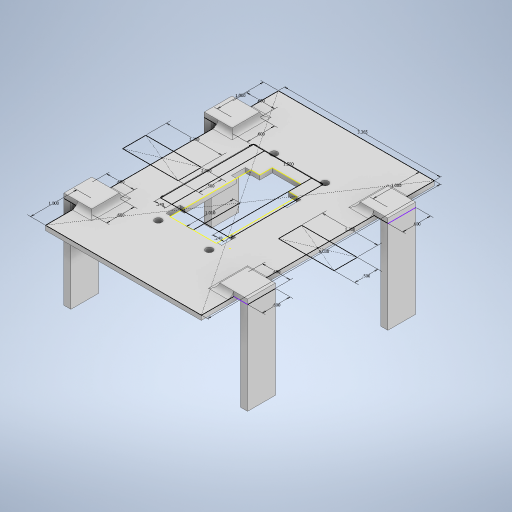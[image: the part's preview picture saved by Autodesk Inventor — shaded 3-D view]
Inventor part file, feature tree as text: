
AUTODESK INVENTOR PART (.ipt)
format: ipt  version: 2024.1 (Build 281209000, 209)  size: 502,272 bytes
history: native  units: in
note: dims shown in document units (in); Inventor stores cm internally (conversion verified against a paired STEP export)
features: extrude x10, sketch x9, projected_geometry x3, hole x2, fillet x2
ambient origin geometry x8: Origin, YZ Plane, XZ Plane, XY Plane, X Axis, Y Axis, Z Axis, Center Point
bodies: Solid1 (feature_tree)
feature tree (26):
  extrude  "Extrusion1"  Depth=2.0in
  extrude  "Extrusion2"  Depth=0.24in
  hole  "Hole1"  [1 undecoded]
  extrude  "Extrusion3"  Depth=1.0in TaperAngle=0.0deg
  extrude  "Extrusion4"  Depth=0.62in
  extrude  "Extrusion5"  Depth=2.02in
  sketch  "Sketch8"  dims[d18=0.5in d19=0.0in d20=0.62in]
  extrude  "Extrusion6"  Depth=1.75in
  sketch  "Sketch6"  dims[d8=0.5in]
  hole  "Hole2"  [1 undecoded]
  fillet  "Fillet1"  Radius=0.25in
  extrude  "Extrusion7"  Depth=0.2in
  extrude  "Extrusion8"  Depth=2.0in
  extrude  "Extrusion9"  Depth=0.2in
  fillet  "Fillet2"  Radius=0.25in
  extrude  "Extrusion10"  Depth=0.2in
  sketch  "Sketch3"  dims[d0=1.5in d1=2.0in]
  projected_geometry  "Projected Loop1"
  sketch  "Sketch4"  dims[d2=0.24in d3=0.24in]
  projected_geometry  "Projected Loop2"
  sketch  "Sketch5"  dims[d4=1.0in d5=0.0in d6=0.2in d7=0.0in]
  sketch  "Sketch7"  dims[d9=0.266in d10=0.75in d11=0.438in d12=0.25in d13=0.5635in d14=1.0in d15=0.8108in d16=0.5in d17=0.0in]
  projected_geometry  "Projected Loop3"
  sketch  "Sketch9"  dims[d21=2.02in d22=0.5in]
  sketch  "Sketch10"  dims[d23=1.75in d24=0.5in]
  sketch  "Sketch12"  dims[d25=0.1in d26=0.0in d27=0.2in d28=0.25in d29=0.2in d30=0.25in d31=0.2in d32=0.25in d33=0.2in d34=0.1495in d35=0.75in d36=0.375in d37=0.25in d38=0.5635in d39=1.0in d40=0.8108in d41=0.125in d42=1.01in d43=3.3654in d44=5.0299in d45=0.1in d46=0.0in d47=0.0in d48=0.0in d49=0.17in d50=0.17in d51=0.2in d52=0.3in d53=0.2in d54=0.3in d55=0.2in d56=0.3in d57=0.2in d58=0.3in d59=1.0in d60=0.0in d61=1.2in d62=0.5in d63=1.2in d64=0.5in d76=0.1in d77=0.0in d78=0.125in d79=1.0in d80=1.0in d81=1.0in d82=0.6in d83=0.6in d84=0.6in d85=0.6in d86=0.6in d87=0.6in d88=0.6in d89=2.0in d90=0.0in]
note: 2 required parameter values undecoded (feature->parameter linkage not recoverable at this tier; creation-order binding heuristic only, values carry confidence <= 0.55)
